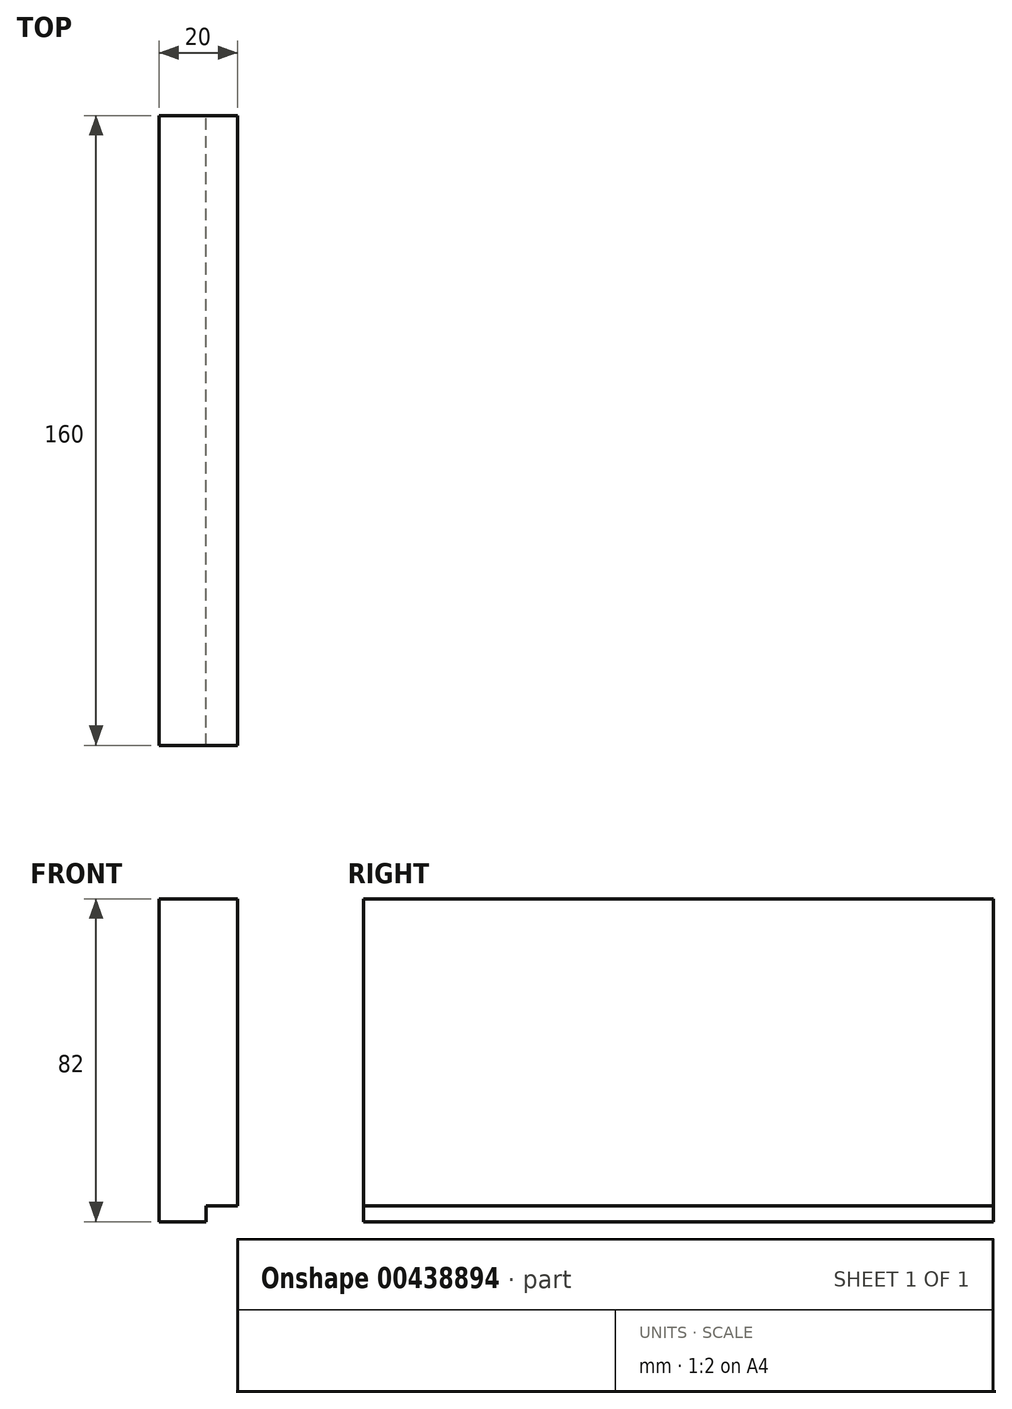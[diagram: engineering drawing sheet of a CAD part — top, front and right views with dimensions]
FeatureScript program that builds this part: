
annotation { "Feature Type Name" : "Feature", "Feature Type Description" : "" }
export const myFeature = defineFeature(function(context is Context, id is Id, definition is map)
    precondition{}
    {
        {
            var Q0;
            Q0=qCreatedBy(makeId("Right.planeOp"),FACE);
            var sketch = newSketch(context, id + "F0", { "sketchPlane" : qUnion([Q0])});
            skLineSegment(sketch, "E0", {"start": v(-80.7, 77.4) * mm, "end": v(79.3, 77.4) * mm});
            skLineSegment(sketch, "E1", {"start": v(79.3, -0.6) * mm, "end": v(79.3, 77.4) * mm});
            skLineSegment(sketch, "E2", {"start": v(-80.7, 77.4) * mm, "end": v(-80.7, -0.6) * mm});
            skLineSegment(sketch, "E3", {"start": v(-80.7, -0.6) * mm, "end": v(79.3, -0.6) * mm});
            skLineSegment(sketch, "E4", {"start": v(-80.7, -0.6) * mm, "end": v(-80.7, -4.6) * mm});
            skLineSegment(sketch, "E5", {"start": v(-80.7, -4.6) * mm, "end": v(79.3, -4.6) * mm});
            skLineSegment(sketch, "E6", {"start": v(79.3, -0.6) * mm, "end": v(79.3, -4.6) * mm});
            skSolve(sketch);
        }
        {
            var Q0;
            Q0=makeQuery(id+"F0.imprint","IMPRINT",FACE,{"disambiguationData":[TD([[makeQuery(id+"F0.imprint","IMPRINT",EDGE,{"derivedFrom":sQuery(id+"F0.wireOp",EDGE,"E0")}),-1.0]])]});
            extrude(context, id + "F1", {"entities" : qUnion([Q0]), "depth" : 20 * mm});
        }
        {
            var Q0;
            Q0=makeQuery(id+"F0.imprint","IMPRINT",FACE,{"disambiguationData":[TD([[makeQuery(id+"F0.imprint","IMPRINT",EDGE,{"derivedFrom":sQuery(id+"F0.wireOp",EDGE,"E0")}),-1.0]])]});
            var Q1;
            Q1=makeQuery(id+"F0.imprint","IMPRINT",FACE,{"disambiguationData":[TD([[makeQuery(id+"F0.imprint","IMPRINT",EDGE,{"derivedFrom":sQuery(id+"F0.wireOp",EDGE,"E3")}),-1.0]])]});
            extrude(context, id + "F2", {"entities" : qUnion([Q0, Q1]), "operationType" : NewBodyOperationType.ADD, "depth" : 12 * mm});
        }
    });
